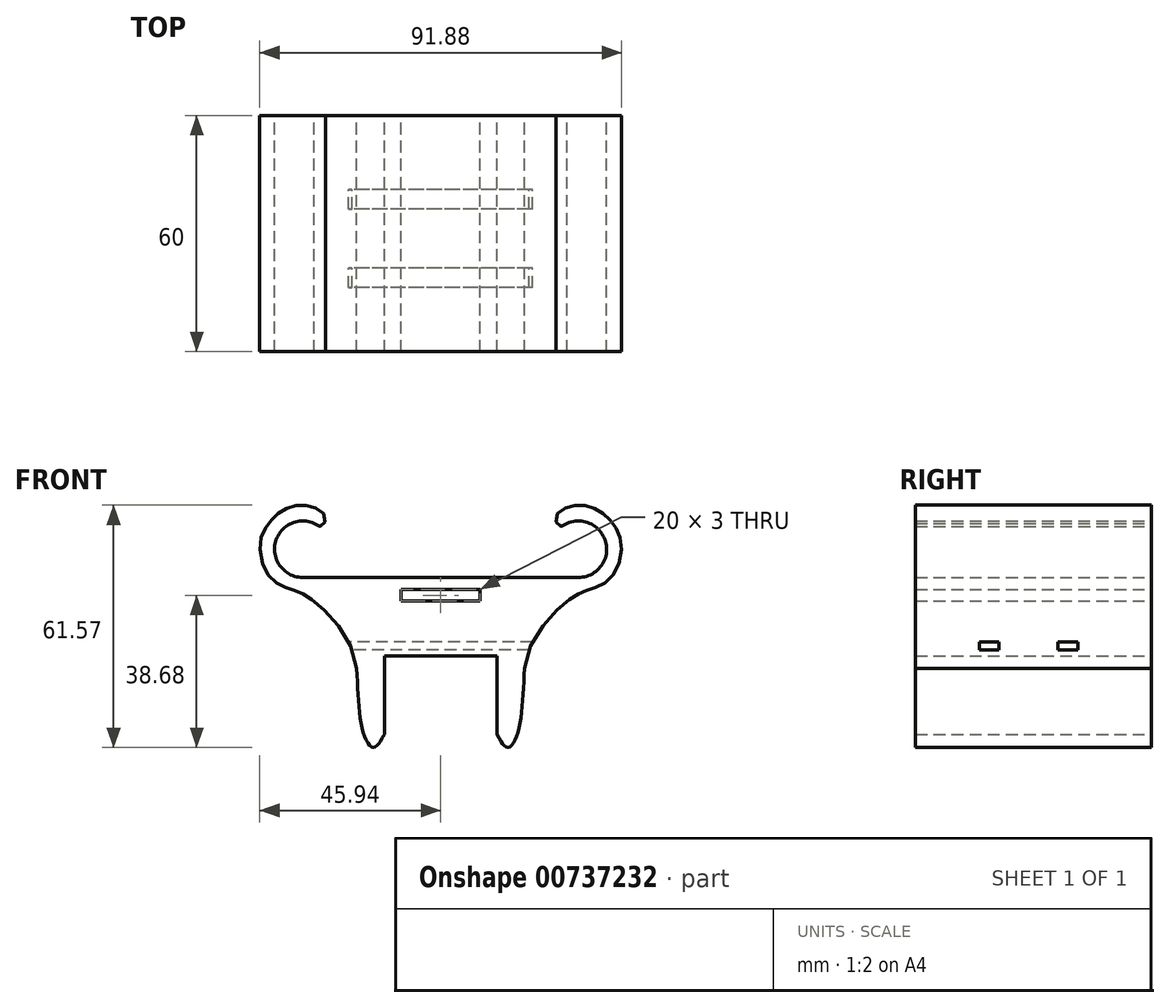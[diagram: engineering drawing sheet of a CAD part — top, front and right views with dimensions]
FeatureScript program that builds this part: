
annotation { "Feature Type Name" : "Feature", "Feature Type Description" : "" }
export const myFeature = defineFeature(function(context is Context, id is Id, definition is map)
    precondition{}
    {
        {
            var Q0;
            Q0=qCreatedBy(makeId("Front.planeOp"),FACE);
            var sketch = newSketch(context, id + "F0", { "sketchPlane" : qUnion([Q0])});
            skLineSegment(sketch, "E0.bottom", {"start": v(0, 0) * mm, "end": v(10, 0) * mm});
            skLineSegment(sketch, "E0.top", {"start": v(0, 3) * mm, "end": v(10, 3) * mm});
            skLineSegment(sketch, "E0.left", {"start": v(0, 0) * mm, "end": v(0, 3) * mm});
            skLineSegment(sketch, "E0.right", {"start": v(10, 0) * mm, "end": v(10, 3) * mm});
            skLineSegment(sketch, "E1", {"start": v(0, 6) * mm, "end": v(35, 6) * mm});
            skArc(sketch, "E2", {"start": v(35, 6) * mm, "mid": v(42.03, 14.63) * mm, "end": v(32.16, 19.78) * mm});
            skFitSpline(sketch, "E3", {"points": [v(32.16, 19.78) * mm, v(30.26, 19) * mm, v(29.33, 21.37) * mm, v(32.16, 23.79) * mm, v(36.54, 24.3) * mm, v(40.68, 22.6) * mm, v(43.66, 19.78) * mm, v(45.81, 15.39) * mm, v(44.4, 7.6) * mm, v(40.13, 3.75) * mm, v(36.26, 2.4) * mm, v(32.16, 0) * mm, v(21.33, -17.15) * mm], "startDerivative": vector(-30.63, -6.27) * mm, "endDerivative": vector(-10.6, -140.44) * mm});
            skLineSegment(sketch, "E4", {"start": v(0, -13.9) * mm, "end": v(14.3, -13.9) * mm});
            skLineSegment(sketch, "E5", {"start": v(14.3, -13.9) * mm, "end": v(14.3, -33.9) * mm});
            skFitSpline(sketch, "E6", {"points": [v(14.3, -33.9) * mm, v(17, -37.18) * mm, v(19.5, -33.9) * mm, v(21.33, -17.15) * mm], "startDerivative": vector(12.87, -21.26) * mm, "endDerivative": vector(2.5, 38.35) * mm});
            skLineSegment(sketch, "E7.MirrorCS", {"start": v(-10, 0) * mm, "end": v(-10, 3) * mm});
            skArc(sketch, "E8.MirrorCS", {"start": v(-35, 6) * mm, "mid": v(-42.03, 14.63) * mm, "end": v(-32.16, 19.78) * mm});
            skLineSegment(sketch, "E9.MirrorCS", {"start": v(0, 0) * mm, "end": v(-10, 0) * mm});
            skLineSegment(sketch, "E10.MirrorCS", {"start": v(0, 6) * mm, "end": v(-35, 6) * mm});
            skFitSpline(sketch, "E11.MirrorCS", {"points": [v(-32.16, 19.78) * mm, v(-30.26, 19) * mm, v(-29.33, 21.37) * mm, v(-32.16, 23.79) * mm, v(-36.54, 24.3) * mm, v(-40.68, 22.6) * mm, v(-43.66, 19.78) * mm, v(-45.81, 15.39) * mm, v(-44.4, 7.6) * mm, v(-40.13, 3.75) * mm, v(-36.26, 2.4) * mm, v(-32.16, 0) * mm, v(-21.33, -17.15) * mm], "startDerivative": vector(30.63, -6.27) * mm, "endDerivative": vector(10.6, -140.44) * mm});
            skLineSegment(sketch, "E12.MirrorCS", {"start": v(-14.3, -13.9) * mm, "end": v(-14.3, -33.9) * mm});
            skLineSegment(sketch, "E13.MirrorCS", {"start": v(0, 3) * mm, "end": v(-10, 3) * mm});
            skLineSegment(sketch, "E14.MirrorCS", {"start": v(0, -13.9) * mm, "end": v(-14.3, -13.9) * mm});
            skFitSpline(sketch, "E15.MirrorCS", {"points": [v(-14.3, -33.9) * mm, v(-17, -37.18) * mm, v(-19.5, -33.9) * mm, v(-21.33, -17.15) * mm], "startDerivative": vector(-12.87, -21.26) * mm, "endDerivative": vector(-2.5, 38.35) * mm});
            skSolve(sketch);
        }
        {
            var Q0;
            Q0 = qSketchRegion(id + "F0", true);
            extrude(context, id + "F1", {"entities" : qUnion([Q0]), "depth" : 60 * mm, "offsetDistance" : 25 * mm});
        }
        {
            var Q0;
            Q0=qCreatedBy(makeId("Right.planeOp"),FACE);
            var sketch = newSketch(context, id + "F2", { "sketchPlane" : qUnion([Q0])});
            skLineSegment(sketch, "E16.bottom", {"start": v(-43.76, -12.38) * mm, "end": v(-38.76, -12.38) * mm});
            skLineSegment(sketch, "E16.top", {"start": v(-43.76, -10.38) * mm, "end": v(-38.76, -10.38) * mm});
            skLineSegment(sketch, "E16.left", {"start": v(-43.76, -12.38) * mm, "end": v(-43.76, -10.38) * mm});
            skLineSegment(sketch, "E16.right", {"start": v(-38.76, -12.38) * mm, "end": v(-38.76, -10.38) * mm});
            skLineSegment(sketch, "E17.bottom", {"start": v(-23.76, -10.38) * mm, "end": v(-18.76, -10.38) * mm});
            skLineSegment(sketch, "E17.top", {"start": v(-23.76, -12.38) * mm, "end": v(-18.76, -12.38) * mm});
            skLineSegment(sketch, "E17.left", {"start": v(-23.76, -10.38) * mm, "end": v(-23.76, -12.38) * mm});
            skLineSegment(sketch, "E17.right", {"start": v(-18.76, -10.38) * mm, "end": v(-18.76, -12.38) * mm});
            skSolve(sketch);
        }
        {
            var Q0;
            Q0 = qSketchRegion(id + "F2", true);
            extrude(context, id + "F3", {"entities" : qUnion([Q0]), "operationType" : NewBodyOperationType.REMOVE, "depth" : 25 * mm, "offsetDistance" : 25 * mm});
        }
        {
            var Q0;
            Q0=makeQuery(id+"F2.imprint","IMPRINT",FACE,{"disambiguationData":[TD([[makeQuery(id+"F2.imprint","IMPRINT",EDGE,{"derivedFrom":sQuery(id+"F2.wireOp",EDGE,"E17.bottom")}),-1.0]])]});
            var Q1;
            Q1=makeQuery(id+"F2.imprint","IMPRINT",FACE,{"disambiguationData":[TD([[makeQuery(id+"F2.imprint","IMPRINT",EDGE,{"derivedFrom":sQuery(id+"F2.wireOp",EDGE,"E16.bottom")}),1.0]])]});
            extrude(context, id + "F4", {"entities" : qUnion([Q0, Q1]), "operationType" : NewBodyOperationType.REMOVE, "oppositeDirection" : true, "depth" : 25 * mm, "offsetDistance" : 25 * mm});
        }
    });
